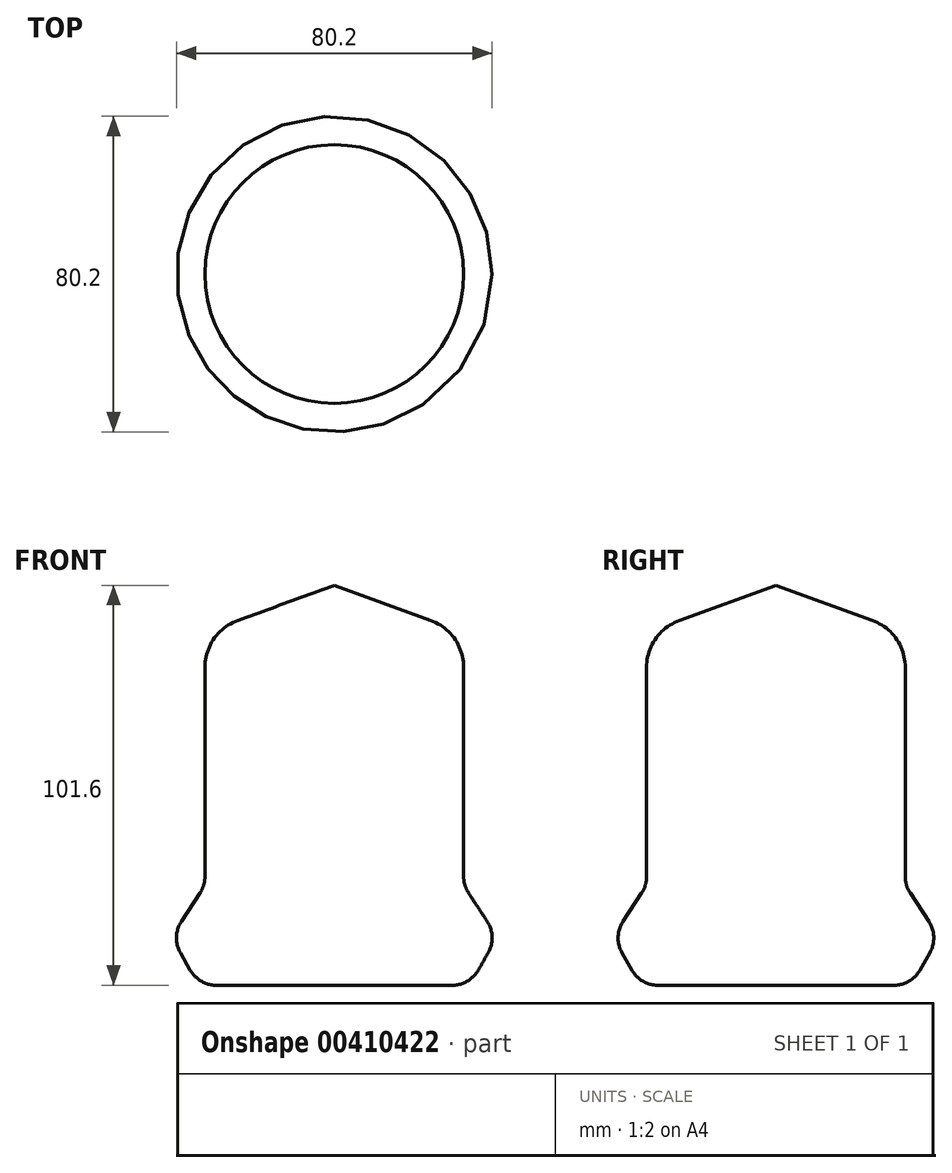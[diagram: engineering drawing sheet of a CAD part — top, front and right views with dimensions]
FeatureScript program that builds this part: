
annotation { "Feature Type Name" : "Feature", "Feature Type Description" : "" }
export const myFeature = defineFeature(function(context is Context, id is Id, definition is map)
    precondition{}
    {
        {
            var Q0;
            Q0=qCreatedBy(makeId("Front.planeOp"),FACE);
            var sketch = newSketch(context, id + "F0", { "sketchPlane" : qUnion([Q0])});
            skLineSegment(sketch, "E0", {"start": v(0, 52.72) * mm, "end": v(0, -48.88) * mm});
            skLineSegment(sketch, "E1", {"start": v(0, 52.72) * mm, "end": v(24.5, 43.8) * mm});
            skLineSegment(sketch, "E2", {"start": v(32.86, 31.87) * mm, "end": v(32.86, -21.26) * mm});
            skLineSegment(sketch, "E3", {"start": v(34.11, -25.44) * mm, "end": v(38.85, -32.67) * mm});
            skLineSegment(sketch, "E4", {"start": v(39.1, -40.64) * mm, "end": v(36.57, -45.04) * mm});
            skLineSegment(sketch, "E5", {"start": v(0, -48.88) * mm, "end": v(29.96, -48.88) * mm});
            skPoint(sketch, "E6.visualSharp", {"position": v(32.86, 40.76) * mm});
            skArc(sketch, "E6.filletArc", {"start": v(32.86, 31.87) * mm, "mid": v(30.57, 39.15) * mm, "end": v(24.5, 43.8) * mm});
            skPoint(sketch, "E7.visualSharp", {"position": v(32.86, -23.54) * mm});
            skArc(sketch, "E7.filletArc", {"start": v(32.86, -21.26) * mm, "mid": v(33.18, -23.44) * mm, "end": v(34.11, -25.44) * mm});
            skPoint(sketch, "E8.visualSharp", {"position": v(41.42, -36.58) * mm});
            skArc(sketch, "E8.filletArc", {"start": v(39.1, -40.64) * mm, "mid": v(40.1, -36.62) * mm, "end": v(38.85, -32.67) * mm});
            skPoint(sketch, "E9.visualSharp", {"position": v(34.38, -48.88) * mm});
            skArc(sketch, "E9.filletArc", {"start": v(29.96, -48.88) * mm, "mid": v(33.78, -47.85) * mm, "end": v(36.57, -45.04) * mm});
            skSolve(sketch);
        }
        {
            var Q0;
            Q0=makeQuery(id+"F0.imprint","IMPRINT",FACE,{"disambiguationData":[TD([[makeQuery(id+"F0.imprint","IMPRINT",EDGE,{"derivedFrom":sQuery(id+"F0.wireOp",EDGE,"E0")}),1.0]])]});
            var Q1;
            Q1=sQuery(id+"F0.wireOp",EDGE,"E0");
            revolve(context, id + "F1", {"entities" : qUnion([Q0]), "axis" : qUnion([Q1]), "revolveType" : RevolveType.FULL});
        }
    });
